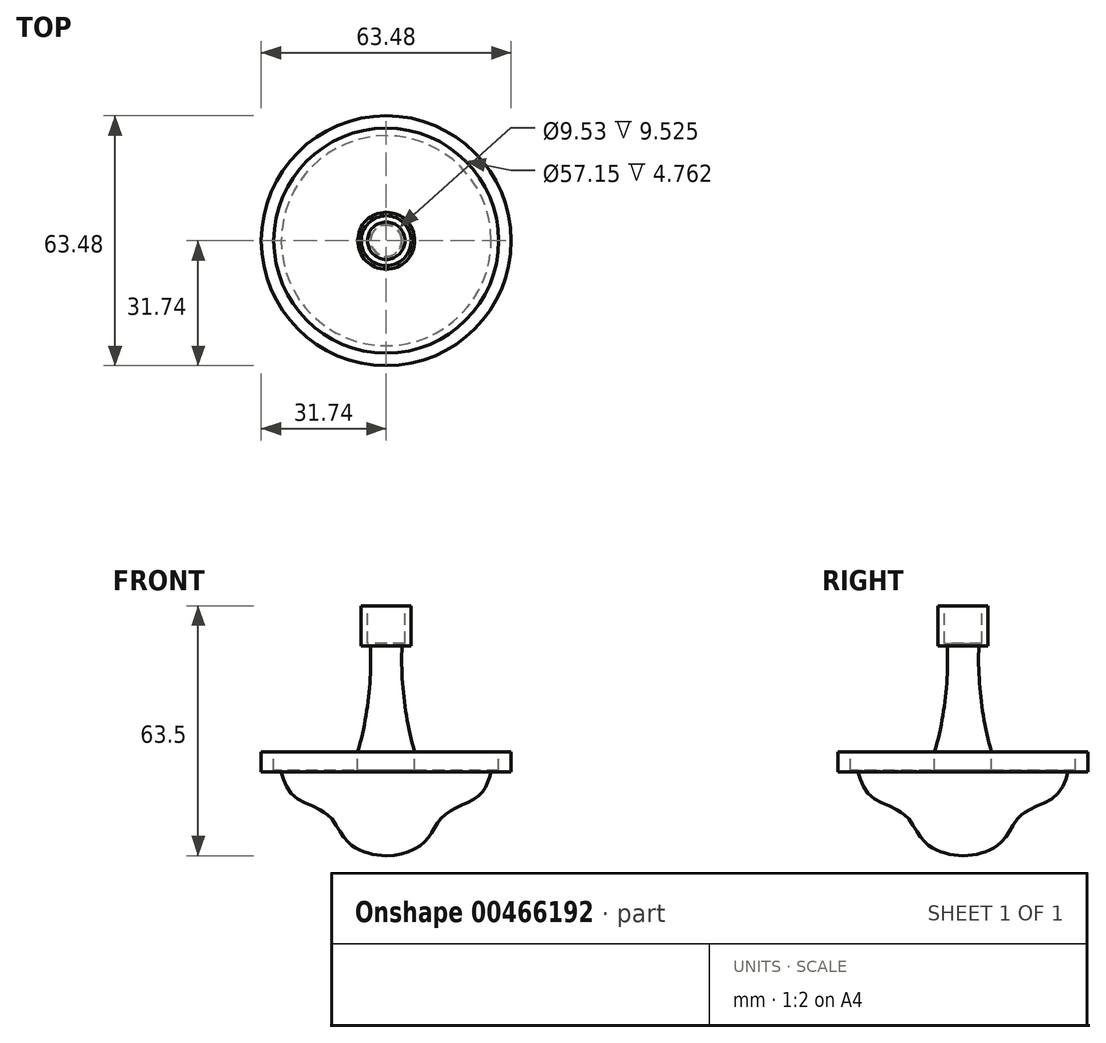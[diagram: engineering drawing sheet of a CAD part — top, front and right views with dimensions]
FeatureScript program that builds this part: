
annotation { "Feature Type Name" : "Feature", "Feature Type Description" : "" }
export const myFeature = defineFeature(function(context is Context, id is Id, definition is map)
    precondition{}
    {
        {
            var Q0;
            Q0=qCreatedBy(makeId("Front.planeOp"),FACE);
            var sketch = newSketch(context, id + "F0", { "sketchPlane" : qUnion([Q0])});
            skLineSegment(sketch, "E0", {"start": v(0, 30.65) * mm, "end": v(0, -32.85) * mm});
            skLineSegment(sketch, "E1", {"start": v(0, 30.65) * mm, "end": v(6.35, 30.65) * mm});
            skLineSegment(sketch, "E2", {"start": v(6.35, 30.65) * mm, "end": v(6.35, 20.49) * mm});
            skLineSegment(sketch, "E3", {"start": v(6.35, 20.49) * mm, "end": v(4.02, 20.49) * mm});
            skArc(sketch, "E4", {"start": v(4.02, 20.49) * mm, "mid": v(4.54, 6.88) * mm, "end": v(7.23, -6.46) * mm});
            skLineSegment(sketch, "E5", {"start": v(7.23, -6.46) * mm, "end": v(31.74, -6.46) * mm});
            skLineSegment(sketch, "E6", {"start": v(31.74, -6.46) * mm, "end": v(31.74, -11.54) * mm});
            skLineSegment(sketch, "E7", {"start": v(31.74, -11.54) * mm, "end": v(26.66, -11.54) * mm});
            skFitSpline(sketch, "E8", {"points": [v(26.66, -11.54) * mm, v(23.27, -17.82) * mm, v(14.8, -22.5) * mm, v(10.12, -28.97) * mm, v(0, -32.85) * mm], "startDerivative": vector(-9.24, -31.9) * mm, "endDerivative": vector(-46.88, -1.05) * mm});
            skSolve(sketch);
        }
        {
            var Q0;
            Q0=makeQuery(id+"F0.imprint","IMPRINT",FACE,{"disambiguationData":[TD([[makeQuery(id+"F0.imprint","IMPRINT",EDGE,{"derivedFrom":sQuery(id+"F0.wireOp",EDGE,"E0")}),1.0]])]});
            var Q1;
            Q1=sQuery(id+"F0.wireOp",EDGE,"E0");
            revolve(context, id + "F1", {"entities" : qUnion([Q0]), "axis" : qUnion([Q1]), "revolveType" : RevolveType.FULL});
        }
        {
            var Q0;
            Q0=makeQuery(id+"F1.opRevolve","SWEPT_FACE",FACE,{"disambiguationData":[OSD([sQuery(id+"F0.wireOp",EDGE,"E1")])]});
            var sketch = newSketch(context, id + "F2", { "sketchPlane" : qUnion([Q0])});
            skCircle(sketch, "E9", {"center": v(0, 0) * mm, "radius": 4.76 * mm});
            skSolve(sketch);
        }
        {
            var Q0;
            Q0=makeQuery(id+"F2.imprint","IMPRINT",FACE,{"disambiguationData":[TD([[makeQuery(id+"F2.imprint","IMPRINT",EDGE,{"derivedFrom":sQuery(id+"F2.wireOp",EDGE,"E9")}),1.0]])]});
            var Q1;
            Q1=sQuery(id+"F2.wireOp",EDGE,"E9");
            extrude(context, id + "F3", {"entities" : qUnion([Q0]), "operationType" : NewBodyOperationType.REMOVE, "surfaceEntities" : qUnion([Q1]), "oppositeDirection" : true, "depth" : 9.52 * mm});
        }
        {
            var Q0;
            Q0=makeQuery(id+"F1.opRevolve","SWEPT_FACE",FACE,{"disambiguationData":[OSD([sQuery(id+"F0.wireOp",EDGE,"E5")])]});
            var sketch = newSketch(context, id + "F4", { "sketchPlane" : qUnion([Q0])});
            skCircle(sketch, "E10", {"center": v(0, 0) * mm, "radius": 28.58 * mm});
            skSolve(sketch);
        }
        {
            var Q0;
            Q0=makeQuery(id+"F4.imprint","IMPRINT",FACE,{"disambiguationData":[TD([[makeQuery(id+"F4.imprint","IMPRINT",EDGE,{"derivedFrom":sQuery(id+"F4.wireOp",EDGE,"E10")}),1.0]])]});
            var Q1;
            Q1=sQuery(id+"F4.wireOp",EDGE,"E10");
            extrude(context, id + "F5", {"entities" : qUnion([Q0]), "operationType" : NewBodyOperationType.REMOVE, "surfaceEntities" : qUnion([Q1]), "oppositeDirection" : true, "depth" : 4.76 * mm});
        }
    });
